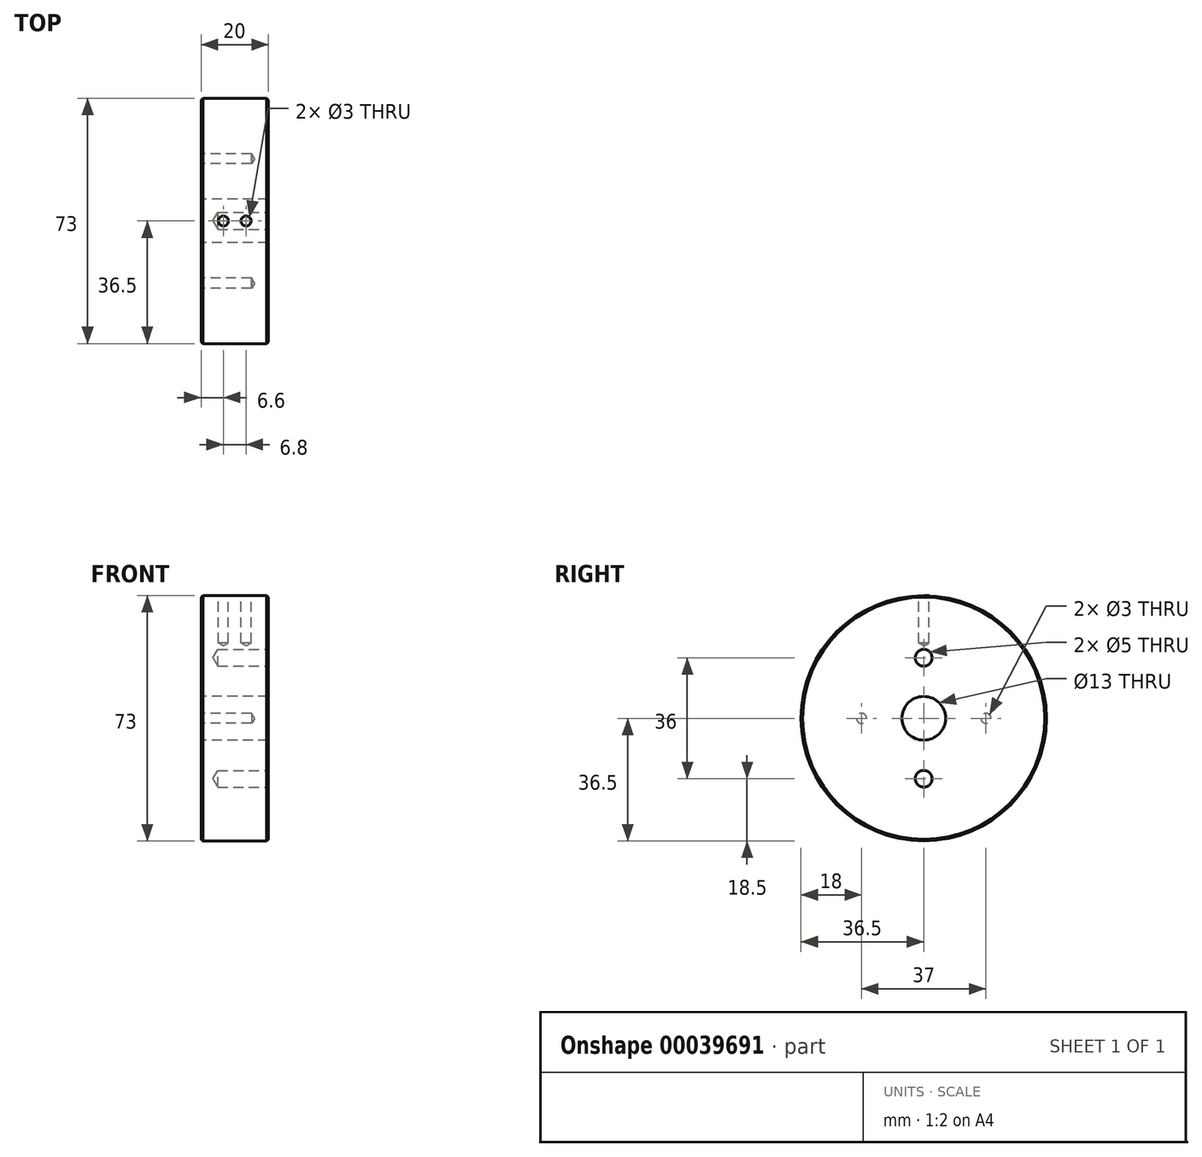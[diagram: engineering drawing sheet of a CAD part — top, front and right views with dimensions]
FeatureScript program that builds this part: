
annotation { "Feature Type Name" : "Feature", "Feature Type Description" : "" }
export const myFeature = defineFeature(function(context is Context, id is Id, definition is map)
    precondition{}
    {
        {
            var Q0;
            Q0=qCreatedBy(makeId("Right.planeOp"),FACE);
            var sketch = newSketch(context, id + "F0", { "sketchPlane" : qUnion([Q0])});
            skCircle(sketch, "E0", {"center": v(0, 0) * mm, "radius": 36.5 * mm});
            skSolve(sketch);
        }
        {
            var Q0;
            Q0=makeQuery(id+"F0.imprint","IMPRINT",FACE,{"disambiguationData":[TD([[makeQuery(id+"F0.imprint","IMPRINT",EDGE,{"derivedFrom":sQuery(id+"F0.wireOp",EDGE,"E0")}),1.0]])]});
            extrude(context, id + "F1", {"entities" : qUnion([Q0]), "depth" : 20 * mm});
        }
        {
            var Q0;
            Q0=makeQuery(id+"F1.opExtrude","CAP_FACE",FACE,{"disambiguationData":[OSD([sQuery(id+"F0.wireOp",EDGE,"E0")])],"isStart":true});
            var sketch = newSketch(context, id + "F2", { "sketchPlane" : qUnion([Q0])});
            skCircle(sketch, "E1", {"center": v(0, 0) * mm, "radius": 6.5 * mm});
            skSolve(sketch);
        }
        {
            var Q0;
            Q0=makeQuery(id+"F2.imprint","IMPRINT",FACE,{"disambiguationData":[TD([[makeQuery(id+"F2.imprint","IMPRINT",EDGE,{"derivedFrom":sQuery(id+"F2.wireOp",EDGE,"E1")}),1.0]])]});
            extrude(context, id + "F3", {"entities" : qUnion([Q0]), "operationType" : NewBodyOperationType.REMOVE, "endBound" : BoundingType.UP_TO_NEXT, "oppositeDirection" : true, "depth" : 25 * mm});
        }
        {
            var Q0;
            Q0=makeQuery(id+"F1.opExtrude","CAP_FACE",FACE,{"disambiguationData":[OSD([sQuery(id+"F0.wireOp",EDGE,"E0")])],"isStart":true});
            var sketch = newSketch(context, id + "F4", { "sketchPlane" : qUnion([Q0])});
            skPoint(sketch, "E2", {"position": v(-18.5, 0) * mm});
            skPoint(sketch, "E3.MirrorP", {"position": v(18.5, 0) * mm});
            skSolve(sketch);
        }
        {
            var Q0;
            Q0=sQuery(id+"F4.wireOp",VERTEX,"E2");
            var Q1;
            Q1=sQuery(id+"F4.wireOp",VERTEX,"E3.MirrorP");
            var Q2;
            Q2=makeQuery(id+"F1.opExtrude","SWEPT_BODY",BODY,{"disambiguationData":[OSD([sQuery(id+"F0.wireOp",EDGE,"E0")])]});
            hole(context, id + "F5", {"style" : HoleStyle.SIMPLE, "holeDiameter" : 3 * mm, "endStyle" : HoleEndStyle.BLIND, "holeDepth" : 15 * mm, "locations" : qUnion([Q0, Q1]), "scope" : qUnion([Q2])});
        }
        {
            var Q0;
            Q0=qCreatedBy(makeId("Top.planeOp"),FACE);
            cPlane(context, id + "F6", {"entities" : qUnion([Q0]), "cplaneType" : CPlaneType.OFFSET, "offset" : (73 / 2) * mm, "width" : 150 * mm, "height" : 150 * mm});
        }
        {
            var Q0;
            Q0=qCreatedBy(id+"F6.planeOp",FACE);
            var sketch = newSketch(context, id + "F7", { "sketchPlane" : qUnion([Q0])});
            skPoint(sketch, "E4", {"position": v(6.6, 0) * mm});
            skPoint(sketch, "E5", {"position": v(13.4, 0) * mm});
            skSolve(sketch);
        }
        {
            var Q0;
            Q0=sQuery(id+"F7.wireOp",VERTEX,"E4");
            var Q1;
            Q1=sQuery(id+"F7.wireOp",VERTEX,"E5");
            var Q2;
            Q2=makeQuery(id+"F1.opExtrude","SWEPT_BODY",BODY,{"disambiguationData":[OSD([sQuery(id+"F0.wireOp",EDGE,"E0")])]});
            hole(context, id + "F8", {"style" : HoleStyle.SIMPLE, "holeDiameter" : 3 * mm, "endStyle" : HoleEndStyle.BLIND, "holeDepth" : 14 * mm, "locations" : qUnion([Q0, Q1]), "scope" : qUnion([Q2])});
        }
        {
            var Q0;
            Q0=makeQuery(id+"F1.opExtrude","CAP_FACE",FACE,{"disambiguationData":[OSD([sQuery(id+"F0.wireOp",EDGE,"E0")])],"isStart":false});
            var sketch = newSketch(context, id + "F9", { "sketchPlane" : qUnion([Q0])});
            skPoint(sketch, "E6", {"position": v(0, 18) * mm});
            skPoint(sketch, "E7.MirrorP", {"position": v(0, -18) * mm});
            skSolve(sketch);
        }
        {
            var Q0;
            Q0=sQuery(id+"F9.wireOp",VERTEX,"E6");
            var Q1;
            Q1=sQuery(id+"F9.wireOp",VERTEX,"E7.MirrorP");
            var Q2;
            Q2=makeQuery(id+"F1.opExtrude","SWEPT_BODY",BODY,{"disambiguationData":[OSD([sQuery(id+"F0.wireOp",EDGE,"E0")])]});
            hole(context, id + "F10", {"style" : HoleStyle.SIMPLE, "holeDiameter" : 5 * mm, "endStyle" : HoleEndStyle.BLIND, "holeDepth" : 15 * mm, "locations" : qUnion([Q0, Q1]), "scope" : qUnion([Q2])});
        }
        {
            var Q0;
            Q0=makeQuery(id+"F1.opExtrude","CAP_EDGE",EDGE,{"disambiguationData":[OSD([sQuery(id+"F0.wireOp",EDGE,"E0")])],"isStart":false});
            var Q1;
            Q1=makeQuery(id+"F1.opExtrude","CAP_EDGE",EDGE,{"disambiguationData":[OSD([sQuery(id+"F0.wireOp",EDGE,"E0")])],"isStart":true});
            var Q2;
            Q2=makeQuery(id+"F3.boolean.opBoolean","COPY",EDGE,{"derivedFrom":makeQuery(id+"F3.opExtrude","CAP_EDGE",EDGE,{"disambiguationData":[OSD([sQuery(id+"F2.wireOp",EDGE,"E1")])],"isStart":true})});
            var Q3;
            Q3=makeQuery(id+"F3.boolean.opBoolean","COPY",EDGE,{"derivedFrom":makeQuery(id+"F3.opExtrude","TWEAK_EDGE",EDGE,{"derivedFrom":[makeQuery(id+"F1.opExtrude","CAP_FACE",FACE,{"disambiguationData":[OSD([sQuery(id+"F0.wireOp",EDGE,"E0")])],"isStart":false}),makeQuery(id+"F2.imprint","IMPRINT",EDGE,{"derivedFrom":sQuery(id+"F2.wireOp",EDGE,"E1")})]})});
            chamfer(context, id + "F11", {"entities" : qUnion([Q0, Q1, Q2, Q3]), "width" : 0.5 * mm, "tangentPropagation" : true});
        }
    });
